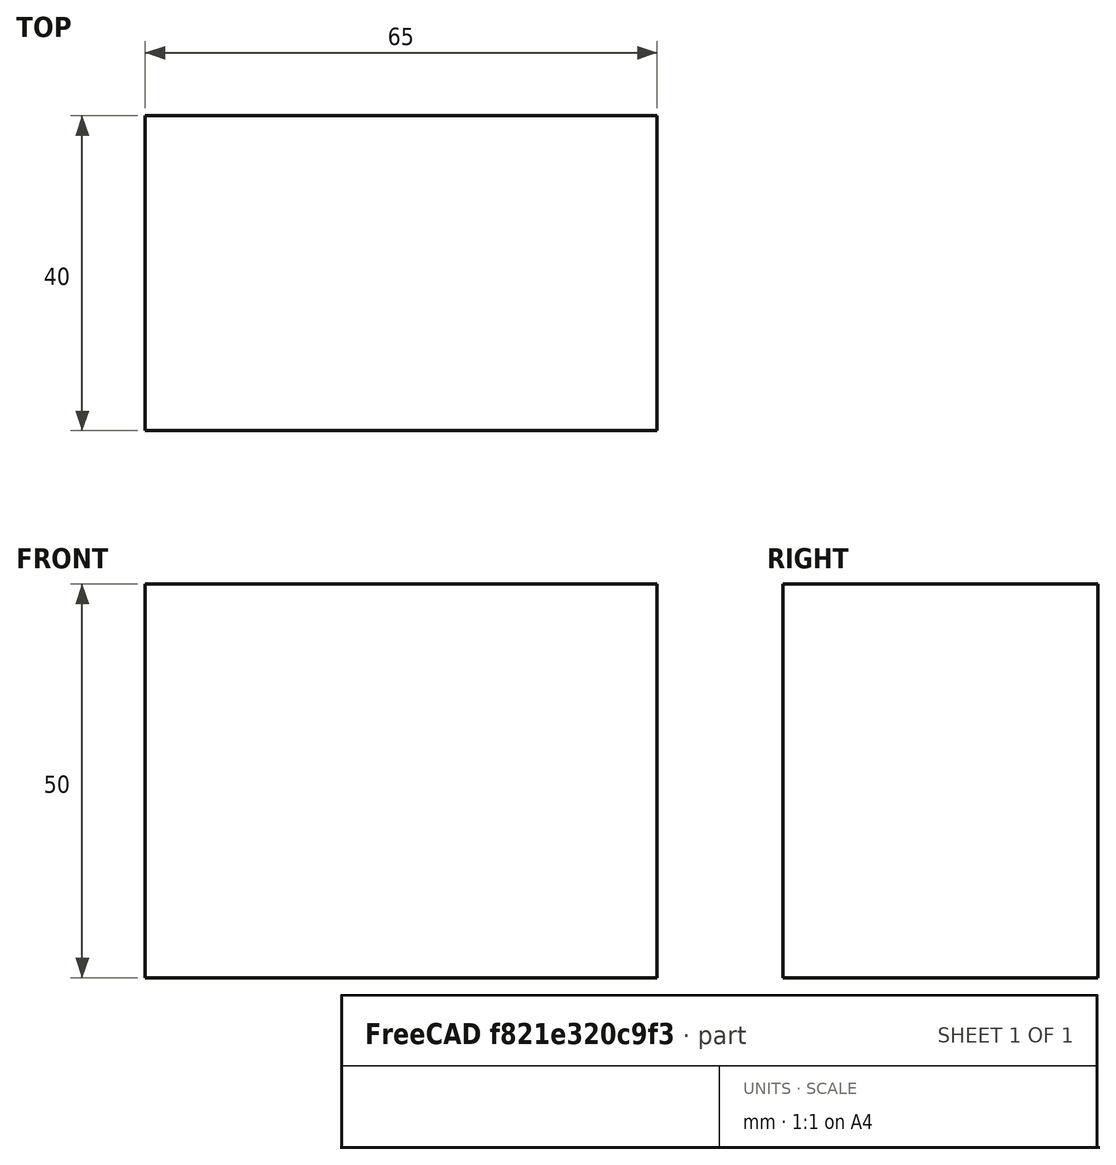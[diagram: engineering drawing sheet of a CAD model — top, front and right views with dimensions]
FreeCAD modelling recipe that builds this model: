
FCSTD DOCUMENT  (FreeCAD 0.15R4671 (Git))
Label: Flat Bar 65x40 EN10058 S235JR
License: All rights reserved
LicenseURL: http://en.wikipedia.org/wiki/All_rights_reserved
objects: Sketcher::SketchObject×1, Part::Extrusion×1
note: 2 computed .brp shape members not serialized (recipe doc carries the construction recipe); baked Part::Feature solids carry a one-line shape summary decoded from their .brp

FEATURE [Sketcher::SketchObject] Sketch
  sketch-geometry (4):
    g0: LineSegment StartX=-32.5 StartY=-20 StartZ=0 EndX=32.5 EndY=-20 EndZ=0
    g1: LineSegment StartX=32.5 StartY=-20 StartZ=0 EndX=32.5 EndY=20 EndZ=0
    g2: LineSegment StartX=32.5 StartY=20 StartZ=0 EndX=-32.5 EndY=20 EndZ=0
    g3: LineSegment StartX=-32.5 StartY=20 StartZ=0 EndX=-32.5 EndY=-20 EndZ=0
  constraints (12):
    c: Coincident(g0,g1)
    c: Coincident(g1,g2)
    c: Coincident(g2,g3)
    c: Coincident(g3,g0)
    c: Horizontal(g0)
    c: Horizontal(g2)
    c: Vertical(g1)
    c: Vertical(g3)
    c: Symmetric(g1,g2,g-2)
    c: Symmetric(g0,g1,g-1)
    c: DistanceY(g1) = 40
    c: DistanceX(g0) = 65
FEATURE [Part::Extrusion] Extrude  label="Flat Bar 65x40 EN10058 S235JR"
  Base = -> Sketch
  Dir = (0,0,50)
  Solid = true
